# Revit family: Faucet-Spray_Kit-KOHLER-Cuff-K-98100ME
name_source: partatom
category: Plumbing Fixtures
units: mm (PartAtom-declared; Revit-internal decimal feet)

## family parameters
Cut with Voids When Loaded = No
Host = Face
Maintain Annotation Orientation = No
OmniClass Number = 23.31.11.00
OmniClass Title = Faucets
Part Type = Normal
Room Calculation Point = No
Round Connector Dimension = Use Diameter
Shared = No

## types (5) — shared parameters
ADA Compliant = No
Assembly Code = D2010
CW Connection = Yes
Cold Water Inlet = Cold Water Inlet
Date Modified = 11/15/2022
Default Elevation = 36"
Description = Health Faucet
Drain Included = No
Faucet Hole Spacing = 0"
Flow Rate = 3 GPM
HW Connection = Yes
Handle Clearance = 0"
Height = 7 1/2"
Hot Water Inlet = Hot Water Inlet
Length = 2 1/8"
Manufacturer = Kohler Co.
Master Format 2014 = 22 41 39
Master Format 2014 Name = Residential Faucets, Supplies, and Trim
Material = Plastic
Pressure = 72.50 psi
Product Name = Cuff
Spout Reach = 0"
URL = https://me.kohler.com
Vent Connection = No
Waste Connection = No
Waste Water Outlet = Waste Water Outlet
WaterSense Certified = No
Width = 1 3/8"

## per-type parameters (varying)
| type | Finish | Model | Type |
| 0-White | Kohler-Plastic-0-White | K-98100ME-0 | 1 |
| BN-Vibrant Brushed Nickel | KOHLER-Plastic-BN-Vibrant_Brushed_Nickel | K-98100ME-BN | 2 |
| BV-Brushed Bronze | Kohler-Plastic-BV-Brushed_Bronze | K-98100ME-BV | 3 |
| CP-Polished Chrome | Kohler-Plastic-CP-Polished_Chrome | K-98100ME-CP | 4 |
| SN-Vibrant Polished Nickel | Kohler-Plastic-SN-Vibrant_Polished_Nickel | K-98100ME-SN | 5 |

## geometry (parser evidence)
native form markers: Sweep x6
no freeform markers — native parametric forms only
